# Revit family: RS 596
name_source: partatom
category: Sanitärinstallationen
units: mm (PartAtom-declared; Revit-internal decimal feet)

## family parameters
Arbeitsebenenbasiert = Nein
Beim Laden mit Abzugskörper schneiden = Nein
Bemaßung runder Anschluss = Durchmesser verwenden
Gemeinsam genutzt = Nein
Immer vertikal = Ja
Raumberechnungspunkt = Nein
Teiletyp = Normal

## types (2) — shared parameters
Abwasserrohrverbindung = Nein
B2 = 336 mm  [stored 1.10236 ft]
Baugruppenkennzeichen = D2030300
HW-Verbindung = Nein
KW-Verbindung = Ja
Lüftungsverbindung = Nein
RS_D110 = 110 mm  [stored 0.360892 ft]
RS_D1d = 120 mm  [stored 0.393701 ft]
RS_Manufacture = Resitec
RS_Sd = 115 mm  [stored 0.377297 ft]
RS_diasenk = 129 mm  [stored 0.423228 ft]
RS_dim001 = 5 mm  [stored 0.0164042 ft]
RS_dim003 = 152 mm
RS_dim009 = 35 mm  [stored 0.114829 ft]
RS_dimDeck = 130 mm  [stored 0.426509 ft]
RS_dimRg = 350 mm  [stored 1.14829 ft]
RS_dimRgL = 200 mm  [stored 0.656168 ft]
RS_dimpfad01 = 315 mm  [stored 1.03346 ft]
RS_s1 = 3 mm  [stored 0.00984252 ft]
RS_s2 = 2 mm  [stored 0.00656168 ft]
URL = https://www.resitec.ch
V max = 230
zero-valued in all types: Vorgabe-Ansicht

## per-type parameters (varying)
| type | Modell |
| DN80 | 100x100 |
| DN100 | RS 596.xx |

note: [stored X ft] marks values corroborated as IEEE doubles in the binary element streams (Revit-internal decimal feet)
